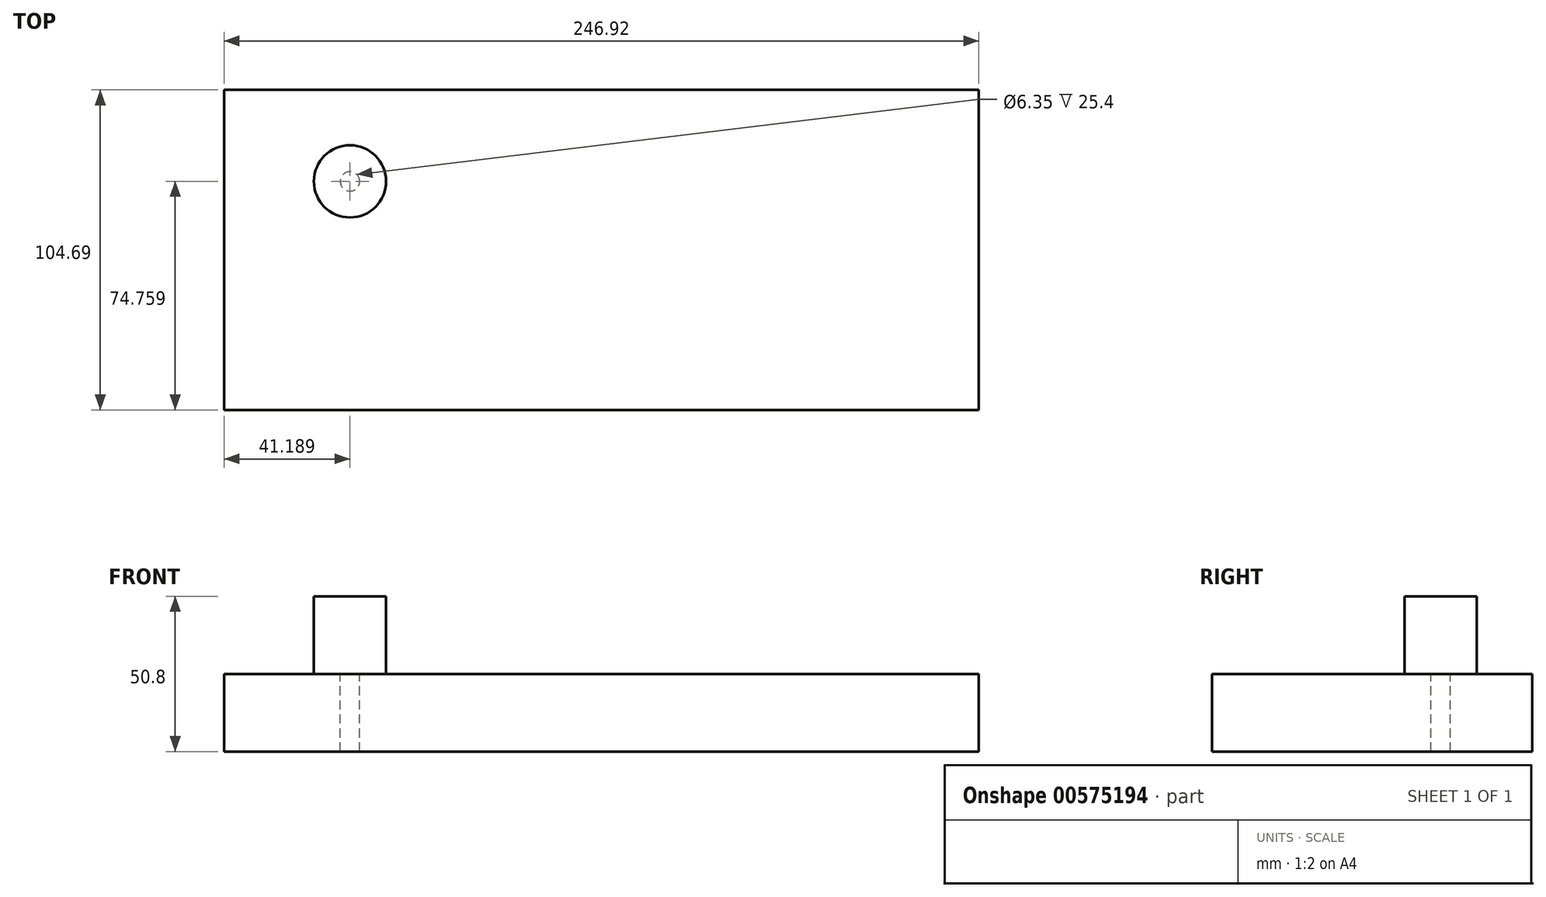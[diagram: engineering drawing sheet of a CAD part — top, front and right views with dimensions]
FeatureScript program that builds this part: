
annotation { "Feature Type Name" : "Feature", "Feature Type Description" : "" }
export const myFeature = defineFeature(function(context is Context, id is Id, definition is map)
    precondition{}
    {
        {
            var Q0;
            Q0=qCreatedBy(makeId("Top.planeOp"),FACE);
            var sketch = newSketch(context, id + "F0", { "sketchPlane" : qUnion([Q0])});
            skLineSegment(sketch, "E0.bottom", {"start": v(-122.46, 56.98) * mm, "end": v(124.46, 56.98) * mm});
            skLineSegment(sketch, "E0.top", {"start": v(-122.46, -47.7) * mm, "end": v(124.46, -47.7) * mm});
            skLineSegment(sketch, "E0.left", {"start": v(-122.46, 56.98) * mm, "end": v(-122.46, -47.7) * mm});
            skLineSegment(sketch, "E0.right", {"start": v(124.46, 56.98) * mm, "end": v(124.46, -47.7) * mm});
            skSolve(sketch);
        }
        {
            var Q0;
            Q0=makeQuery(id+"F0.imprint","IMPRINT",FACE,{"disambiguationData":[TD([[makeQuery(id+"F0.imprint","IMPRINT",EDGE,{"derivedFrom":sQuery(id+"F0.wireOp",EDGE,"E0.bottom")}),-1.0]])]});
            extrude(context, id + "F1", {"entities" : qUnion([Q0]), "depth" : 25.4 * mm, "offsetDistance" : 25.4 * mm});
        }
        {
            var Q0;
            Q0=makeQuery(id+"F1.opExtrude","CAP_FACE",FACE,{"disambiguationData":[OSD([sQuery(id+"F0.wireOp",EDGE,"E0.bottom"),sQuery(id+"F0.wireOp",EDGE,"E0.top"),sQuery(id+"F0.wireOp",EDGE,"E0.left"),sQuery(id+"F0.wireOp",EDGE,"E0.right")])],"isStart":false});
            var sketch = newSketch(context, id + "F2", { "sketchPlane" : qUnion([Q0])});
            skCircle(sketch, "E1", {"center": v(-81.27, 27.05) * mm, "radius": 11.81 * mm});
            skSolve(sketch);
        }
        {
            var Q0;
            Q0=sQuery(id+"F2.wireOp",VERTEX,"E1.center");
            var Q1;
            Q1=makeQuery(id+"F1.opExtrude","SWEPT_BODY",BODY,{"disambiguationData":[OSD([sQuery(id+"F0.wireOp",EDGE,"E0.bottom"),sQuery(id+"F0.wireOp",EDGE,"E0.top"),sQuery(id+"F0.wireOp",EDGE,"E0.left"),sQuery(id+"F0.wireOp",EDGE,"E0.right")])]});
            hole(context, id + "F3", {"style" : HoleStyle.SIMPLE, "endStyle" : HoleEndStyle.THROUGH, "holeDiameter" : 6.35 * mm, "isTappedThrough" : true, "tappedDepth" : 12.7 * mm, "tapClearance" : 3, "locations" : qUnion([Q0]), "scope" : qUnion([Q1])});
        }
        {
            var Q0;
            Q0 = qSketchRegion(id + "F2", true);
            extrude(context, id + "F4", {"entities" : qUnion([Q0]), "operationType" : NewBodyOperationType.ADD, "depth" : 25.4 * mm, "offsetDistance" : 25.4 * mm});
        }
    });
